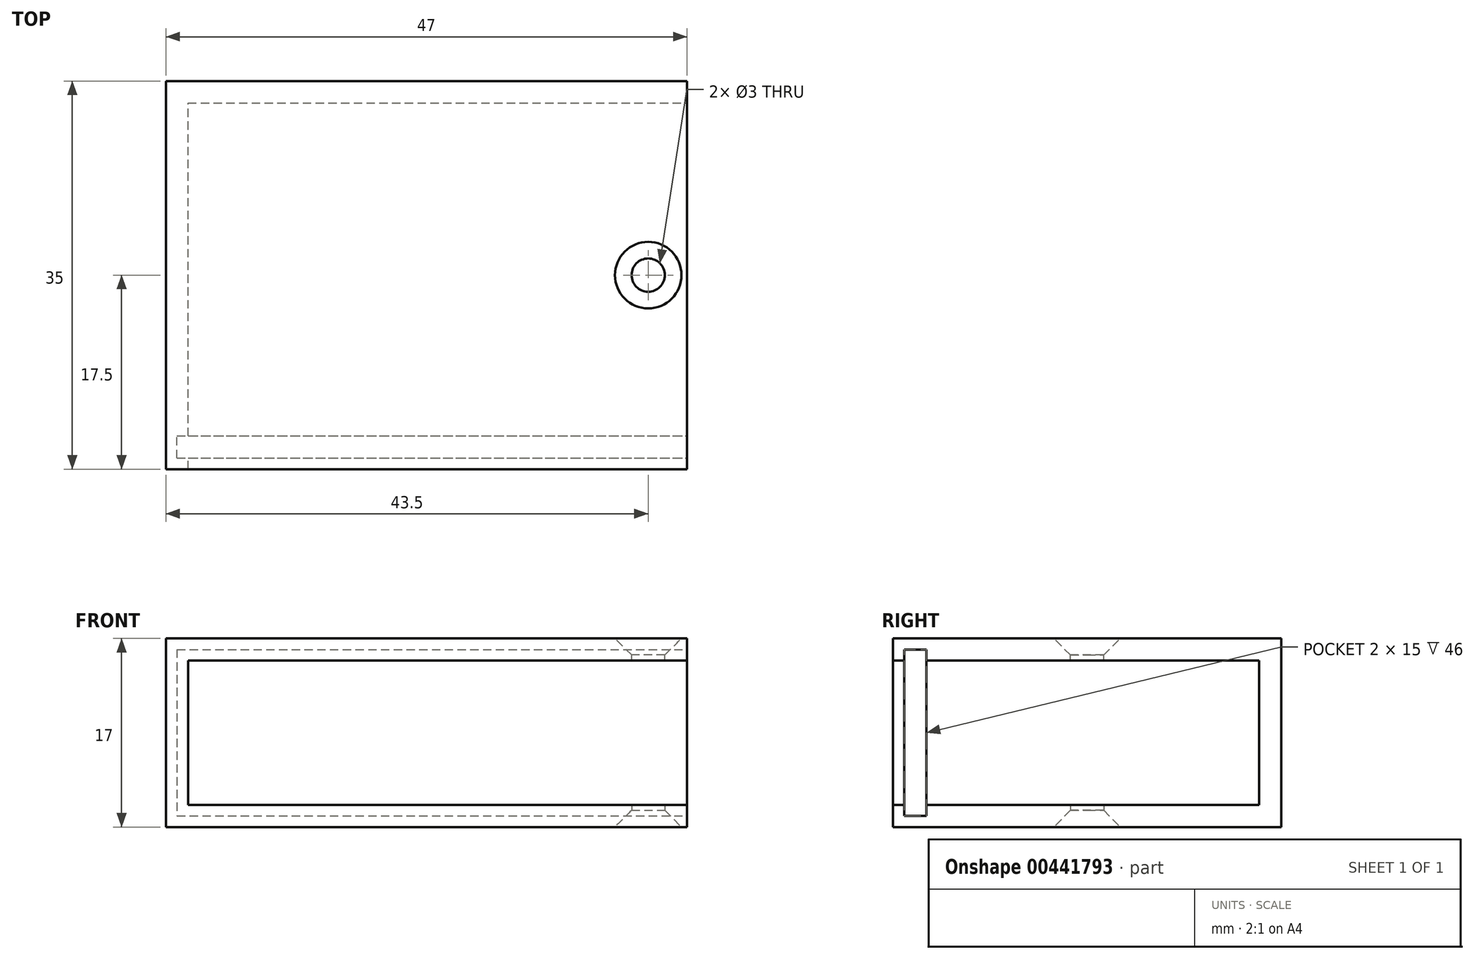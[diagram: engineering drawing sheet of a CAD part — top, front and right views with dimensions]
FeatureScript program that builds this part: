
annotation { "Feature Type Name" : "Feature", "Feature Type Description" : "" }
export const myFeature = defineFeature(function(context is Context, id is Id, definition is map)
    precondition{}
    {
        {
            var Q0;
            Q0=qCreatedBy(makeId("Right.planeOp"),FACE);
            var sketch = newSketch(context, id + "F0", { "sketchPlane" : qUnion([Q0])});
            skLineSegment(sketch, "E0.bottom", {"start": v(17.5, -8.5) * mm, "end": v(-17.5, -8.5) * mm});
            skLineSegment(sketch, "E0.top", {"start": v(17.5, 8.5) * mm, "end": v(-17.5, 8.5) * mm});
            skLineSegment(sketch, "E0.left", {"start": v(17.5, -8.5) * mm, "end": v(17.5, 8.5) * mm});
            skLineSegment(sketch, "E0.right", {"start": v(-17.5, -8.5) * mm, "end": v(-17.5, 8.5) * mm});
            skPoint(sketch, "E0.middle", {"position": v(0, 0) * mm});
            skSolve(sketch);
        }
        {
            var Q0;
            Q0 = qSketchRegion(id + "F0", true);
            extrude(context, id + "F1", {"entities" : qUnion([Q0]), "depth" : 47 * mm});
        }
        {
            var Q0;
            Q0=makeQuery(id+"F1.opExtrude","CAP_FACE",FACE,{"disambiguationData":[OSD([sQuery(id+"F0.wireOp",EDGE,"E0.bottom"),sQuery(id+"F0.wireOp",EDGE,"E0.top"),sQuery(id+"F0.wireOp",EDGE,"E0.left"),sQuery(id+"F0.wireOp",EDGE,"E0.right")])],"isStart":false});
            var sketch = newSketch(context, id + "F2", { "sketchPlane" : qUnion([Q0])});
            skLineSegment(sketch, "E1.bottom", {"start": v(-16.5, 7.5) * mm, "end": v(-14.5, 7.5) * mm});
            skLineSegment(sketch, "E1.top", {"start": v(-16.5, -7.5) * mm, "end": v(-14.5, -7.5) * mm});
            skLineSegment(sketch, "E1.left", {"start": v(-16.5, 7.5) * mm, "end": v(-16.5, -7.5) * mm});
            skLineSegment(sketch, "E1.right", {"start": v(-14.5, 7.5) * mm, "end": v(-14.5, -7.5) * mm});
            skLineSegment(sketch, "E2.bottom", {"start": v(-17.5, 6.5) * mm, "end": v(15.5, 6.5) * mm});
            skLineSegment(sketch, "E2.top", {"start": v(-17.5, -6.5) * mm, "end": v(15.5, -6.5) * mm});
            skLineSegment(sketch, "E2.left", {"start": v(-17.5, 6.5) * mm, "end": v(-17.5, -6.5) * mm});
            skLineSegment(sketch, "E2.right", {"start": v(15.5, 6.5) * mm, "end": v(15.5, -6.5) * mm});
            skSolve(sketch);
        }
        {
            var Q0;
            {var subQ5=sQuery(id+"F2.wireOp",EDGE,"E2.right");Q0=makeQuery(id+"F2.imprint","IMPRINT",FACE,{"disambiguationData":[TD([[makeQuery(id+"F2.imprint","IMPRINT",EDGE,{"derivedFrom":subQ5}),-1.0]])]});}
            var Q1;
            {var subQ5=sQuery(id+"F2.wireOp",EDGE,"E2.left");Q1=makeQuery(id+"F2.imprint","IMPRINT",FACE,{"disambiguationData":[TD([[makeQuery(id+"F2.imprint","IMPRINT",EDGE,{"derivedFrom":subQ5}),-1.0]])]});}
            extrude(context, id + "F3", {"entities" : qUnion([Q0, Q1]), "operationType" : NewBodyOperationType.REMOVE, "oppositeDirection" : true, "depth" : 45 * mm});
        }
        {
            var Q0;
            {var subQ0=sQuery(id+"F2.wireOp",EDGE,"E2.bottom");var subQ1=sQuery(id+"F2.wireOp",EDGE,"E1.left");var subQ2=makeQuery(id+"F2.imprint","INTERSECT",VERTEX,{"derivedFrom":[subQ1,subQ0]});Q0=makeQuery(id+"F2.imprint","IMPRINT",FACE,{"disambiguationData":[TD([[makeQuery(id+"F2.imprint","IMPRINT",EDGE,{"disambiguationData":[TD([[subQ2,-1.0]])],"derivedFrom":subQ1}),1.0]])]});}
            var Q1;
            {var subQ0=sQuery(id+"F2.wireOp",EDGE,"E1.bottom");Q1=makeQuery(id+"F2.imprint","IMPRINT",FACE,{"disambiguationData":[TD([[makeQuery(id+"F2.imprint","IMPRINT",EDGE,{"derivedFrom":subQ0}),-1.0]])]});}
            var Q2;
            {var subQ0=sQuery(id+"F2.wireOp",EDGE,"E1.top");Q2=makeQuery(id+"F2.imprint","IMPRINT",FACE,{"disambiguationData":[TD([[makeQuery(id+"F2.imprint","IMPRINT",EDGE,{"derivedFrom":subQ0}),1.0]])]});}
            extrude(context, id + "F4", {"entities" : qUnion([Q0, Q1, Q2]), "operationType" : NewBodyOperationType.REMOVE, "oppositeDirection" : true, "depth" : 46 * mm});
        }
        {
            var Q0;
            Q0=makeQuery(id+"F1.opExtrude","SWEPT_FACE",FACE,{"disambiguationData":[OSD([sQuery(id+"F0.wireOp",EDGE,"E0.top")])]});
            var sketch = newSketch(context, id + "F5", { "sketchPlane" : qUnion([Q0])});
            skPoint(sketch, "E3", {"position": v(43.5, 0) * mm});
            skSolve(sketch);
        }
        {
            var Q0;
            Q0=sQuery(id+"F5.wireOp",VERTEX,"E3");
            var Q1;
            Q1=makeQuery(id+"F1.opExtrude","SWEPT_BODY",BODY,{"disambiguationData":[OSD([sQuery(id+"F0.wireOp",EDGE,"E0.bottom"),sQuery(id+"F0.wireOp",EDGE,"E0.top"),sQuery(id+"F0.wireOp",EDGE,"E0.left"),sQuery(id+"F0.wireOp",EDGE,"E0.right")])]});
            hole(context, id + "F6", {"style" : HoleStyle.C_SINK, "endStyle" : HoleEndStyle.BLIND, "holeDiameter" : 3 * mm, "cSinkDiameter" : 6 * mm, "cSinkAngle" : 90 * degree, "holeDepth" : 3 * mm, "isTappedThrough" : true, "tappedDepth" : 12 * mm, "tapClearance" : 3, "startFromSketch" : true, "locations" : qUnion([Q0]), "scope" : qUnion([Q1])});
        }
        {
            var Q0;
            Q0=makeQuery(id+"F1.opExtrude","SWEPT_FACE",FACE,{"disambiguationData":[OSD([sQuery(id+"F0.wireOp",EDGE,"E0.bottom")])]});
            var sketch = newSketch(context, id + "F7", { "sketchPlane" : qUnion([Q0])});
            skPoint(sketch, "E4", {"position": v(43.5, 0) * mm});
            skSolve(sketch);
        }
        {
            var Q0;
            Q0=sQuery(id+"F7.wireOp",VERTEX,"E4");
            var Q1;
            Q1=makeQuery(id+"F1.opExtrude","SWEPT_BODY",BODY,{"disambiguationData":[OSD([sQuery(id+"F0.wireOp",EDGE,"E0.bottom"),sQuery(id+"F0.wireOp",EDGE,"E0.top"),sQuery(id+"F0.wireOp",EDGE,"E0.left"),sQuery(id+"F0.wireOp",EDGE,"E0.right")])]});
            hole(context, id + "F8", {"style" : HoleStyle.C_SINK, "endStyle" : HoleEndStyle.BLIND, "holeDiameter" : 3 * mm, "cSinkDiameter" : 6 * mm, "cSinkAngle" : 90 * degree, "holeDepth" : 3 * mm, "isTappedThrough" : true, "tappedDepth" : 12 * mm, "tapClearance" : 3, "startFromSketch" : true, "locations" : qUnion([Q0]), "scope" : qUnion([Q1])});
        }
    });
